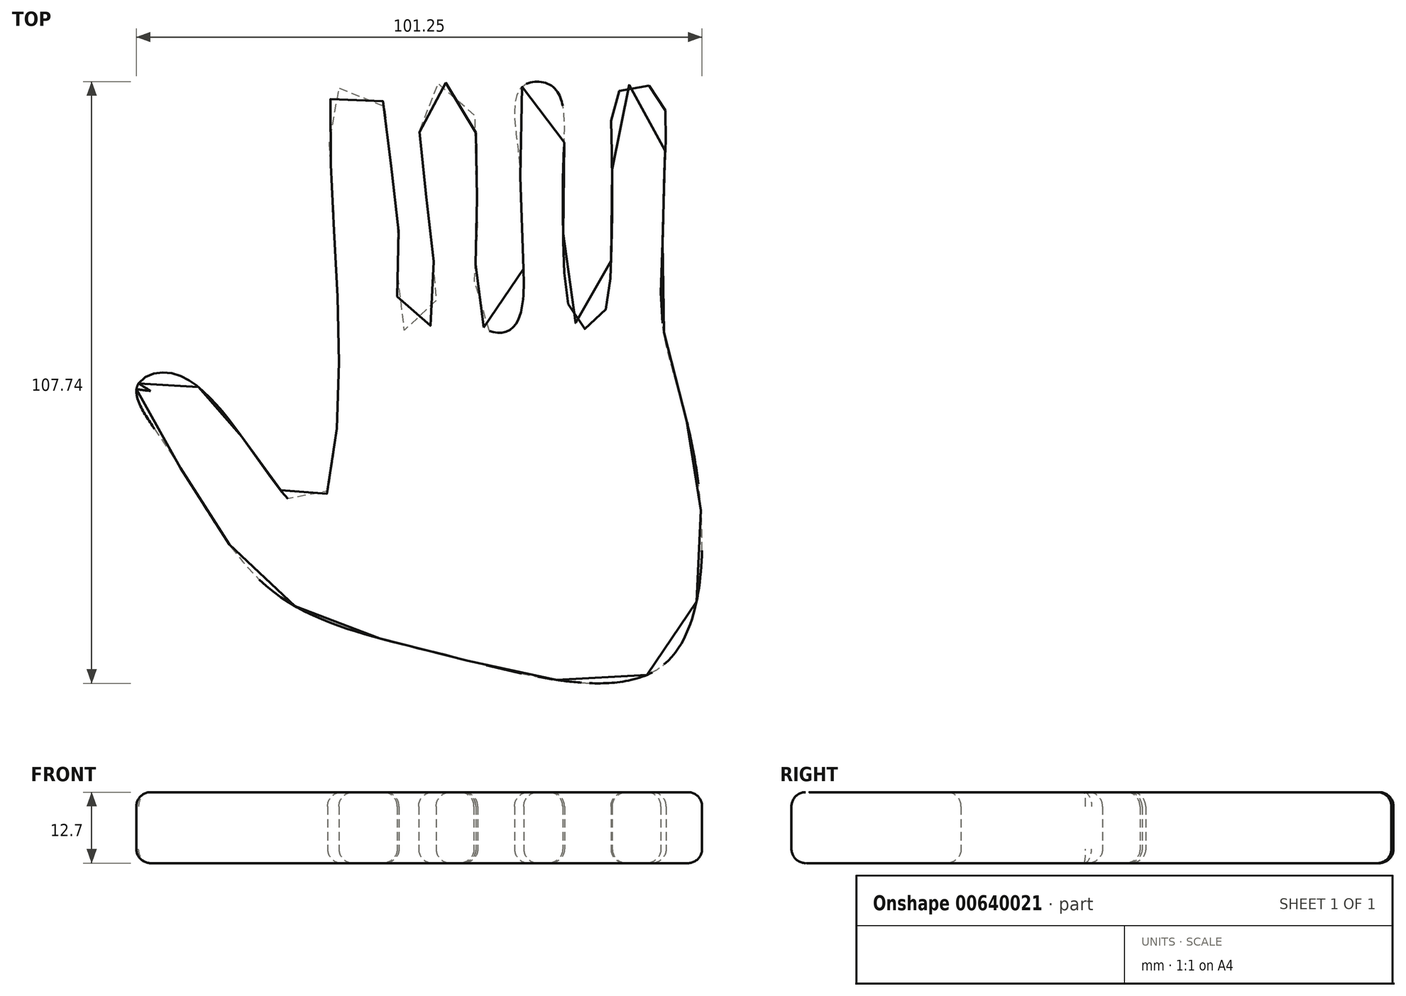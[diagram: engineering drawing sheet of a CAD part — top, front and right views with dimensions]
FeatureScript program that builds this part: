
annotation { "Feature Type Name" : "Feature", "Feature Type Description" : "" }
export const myFeature = defineFeature(function(context is Context, id is Id, definition is map)
    precondition{}
    {
        {
            var Q0;
            Q0=qCreatedBy(makeId("Top.planeOp"),FACE);
            var sketch = newSketch(context, id + "F0", { "sketchPlane" : qUnion([Q0])});
            skFitSpline(sketch, "E0", {"points": [v(0, -27.86) * mm, v(-31.78, -15.83) * mm, v(-49.2, 8.22) * mm, v(-55.34, 20.25) * mm, v(-49.45, 22.7) * mm, v(-36.2, 10.68) * mm, v(-23.44, -2.33) * mm, v(-19.27, 30.56) * mm, v(-20, 45.77) * mm, v(-20.74, 60.99) * mm, v(-19.76, 73.26) * mm, v(-12.64, 73.26) * mm, v(-9.94, 60) * mm, v(-8.47, 46.26) * mm, v(-7.49, 30.31) * mm, v(-3.07, 30.8) * mm, v(-2.82, 47) * mm, v(-4.3, 61.48) * mm, v(-3.56, 73.5) * mm, v(3.31, 73.26) * mm, v(5.28, 61.23) * mm, v(5.52, 45.53) * mm, v(6.26, 31.3) * mm, v(11.9, 30.8) * mm, v(13.62, 45.77) * mm, v(12.89, 62.22) * mm, v(13.38, 73.75) * mm, v(19.27, 73.75) * mm, v(20.98, 61.48) * mm, v(20.98, 44.3) * mm, v(23.44, 31.3) * mm, v(27.12, 31.3) * mm, v(29.57, 45.04) * mm, v(29.57, 62.7) * mm, v(31.3, 73.5) * mm, v(37.67, 73.26) * mm, v(39.15, 62.22) * mm, v(38.66, 44.8) * mm, v(38.9, 30.07) * mm, v(44.55, 6.75) * mm, v(38.9, -29.57) * mm, v(0, -27.86) * mm]});
            skSolve(sketch);
        }
        {
            var Q0;
            Q0=makeQuery(id+"F0.imprint","IMPRINT",FACE,{"disambiguationData":[TD([[makeQuery(id+"F0.imprint","IMPRINT",EDGE,{"derivedFrom":sQuery(id+"F0.wireOp",EDGE,"E0")}),-1.0]])]});
            extrude(context, id + "F1", {"entities" : qUnion([Q0]), "endBound" : BoundingType.SYMMETRIC, "depth" : 12.7 * mm, "offsetDistance" : 25.4 * mm});
        }
        {
            var Q0;
            Q0=makeQuery(id+"F1.opExtrude","SWEPT_FACE",FACE,{"disambiguationData":[OSD([sQuery(id+"F0.wireOp",EDGE,"E0")])]});
            var Q1;
            Q1=makeQuery(id+"F1.opExtrude","CAP_FACE",FACE,{"disambiguationData":[OSD([sQuery(id+"F0.wireOp",EDGE,"E0")])],"isStart":false});
            fillet(context, id + "F2", {"entities" : qUnion([Q0, Q1]), "radius" : 2.54 * mm, "tangentPropagation" : true, "allowEdgeOverflow" : false});
        }
    });
